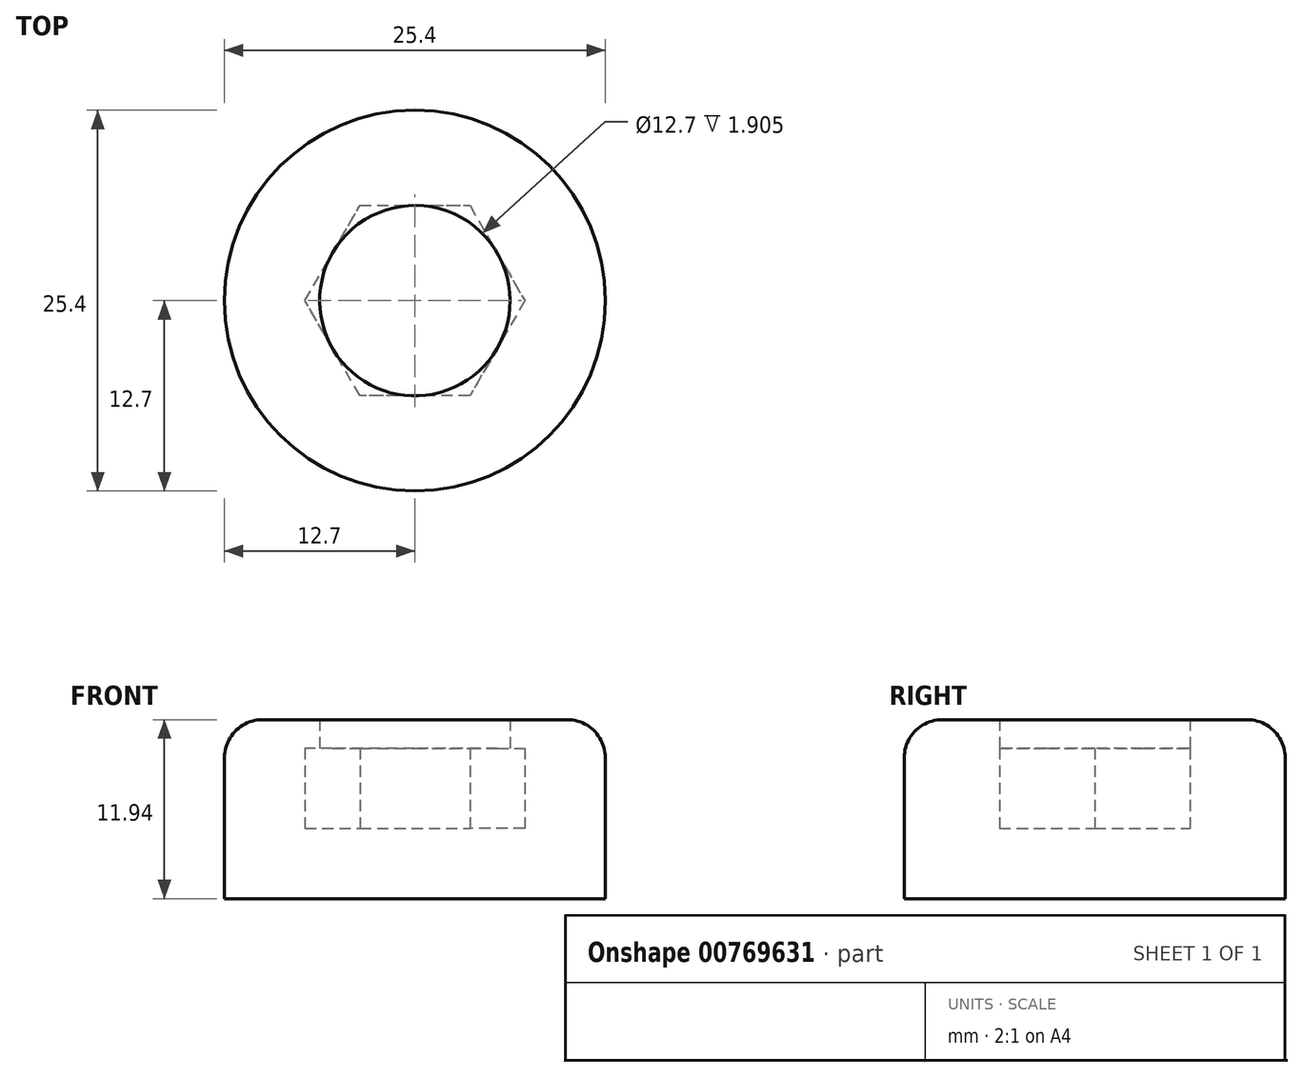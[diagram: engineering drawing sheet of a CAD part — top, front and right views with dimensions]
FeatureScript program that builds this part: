
annotation { "Feature Type Name" : "Feature", "Feature Type Description" : "" }
export const myFeature = defineFeature(function(context is Context, id is Id, definition is map)
    precondition{}
    {
        {
            var Q0;
            Q0=qCreatedBy(makeId("Top.planeOp"),FACE);
            var sketch = newSketch(context, id + "F0", { "sketchPlane" : qUnion([Q0])});
            skCircle(sketch, "E0.cCircle", {"center": v(0, 0) * mm, "radius": 6.35 * mm, "construction": true});
            skLineSegment(sketch, "E0.0", {"start": v(3.67, 6.35) * mm, "end": v(7.33, 0) * mm});
            skLineSegment(sketch, "E0.1", {"start": v(7.33, 0) * mm, "end": v(3.67, -6.35) * mm});
            skLineSegment(sketch, "E0.2", {"start": v(3.67, -6.35) * mm, "end": v(-3.67, -6.35) * mm});
            skLineSegment(sketch, "E0.3", {"start": v(-3.67, -6.35) * mm, "end": v(-7.33, 0) * mm});
            skLineSegment(sketch, "E0.4", {"start": v(-7.33, 0) * mm, "end": v(-3.67, 6.35) * mm});
            skLineSegment(sketch, "E0.5", {"start": v(-3.67, 6.35) * mm, "end": v(3.67, 6.35) * mm});
            skPoint(sketch, "E0.0.midPoint", {"position": v(5.5, 3.18) * mm});
            skCircle(sketch, "E1", {"center": v(0, 0) * mm, "radius": 12.7 * mm});
            skSolve(sketch);
        }
        {
            var Q0;
            Q0=makeQuery(id+"F0.imprint","IMPRINT",FACE,{"disambiguationData":[TD([[makeQuery(id+"F0.imprint","IMPRINT",EDGE,{"derivedFrom":sQuery(id+"F0.wireOp",EDGE,"E0.0")}),1.0]])]});
            var Q1;
            Q1=makeQuery(id+"F0.imprint","IMPRINT",FACE,{"disambiguationData":[TD([[makeQuery(id+"F0.imprint","IMPRINT",EDGE,{"derivedFrom":sQuery(id+"F0.wireOp",EDGE,"E0.0")}),-1.0]])]});
            extrude(context, id + "F1", {"entities" : qUnion([Q0, Q1]), "oppositeDirection" : true, "depth" : 4.7 * mm, "offsetDistance" : 25.4 * mm});
        }
        {
            var Q0;
            Q0=makeQuery(id+"F0.imprint","IMPRINT",FACE,{"disambiguationData":[TD([[makeQuery(id+"F0.imprint","IMPRINT",EDGE,{"derivedFrom":sQuery(id+"F0.wireOp",EDGE,"E0.0")}),1.0]])]});
            extrude(context, id + "F2", {"entities" : qUnion([Q0]), "operationType" : NewBodyOperationType.ADD, "depth" : 5.33 * mm, "offsetDistance" : 25.4 * mm});
        }
        {
            var Q0;
            Q0=makeQuery(id+"F2.opExtrude","CAP_FACE",FACE,{"disambiguationData":[OSD([sQuery(id+"F0.wireOp",EDGE,"E0.0"),sQuery(id+"F0.wireOp",EDGE,"E0.1"),sQuery(id+"F0.wireOp",EDGE,"E0.2"),sQuery(id+"F0.wireOp",EDGE,"E0.3"),sQuery(id+"F0.wireOp",EDGE,"E0.4"),sQuery(id+"F0.wireOp",EDGE,"E0.5"),sQuery(id+"F0.wireOp",EDGE,"E1")])],"isStart":false});
            var sketch = newSketch(context, id + "F3", { "sketchPlane" : qUnion([Q0])});
            skCircle(sketch, "E2", {"center": v(0, 0) * mm, "radius": 6.35 * mm});
            skSolve(sketch);
        }
        {
            var Q0;
            Q0=makeQuery(id+"F3.imprint","IMPRINT",FACE,{"disambiguationData":[TD([[makeQuery(id+"F3.imprint","IMPRINT",EDGE,{"derivedFrom":makeQuery(id+"F2.opExtrude","CAP_EDGE",EDGE,{"disambiguationData":[OSD([sQuery(id+"F0.wireOp",EDGE,"E1")])],"isStart":false})}),1.0]])]});
            var Q1;
            {var subQ0=sQuery(id+"F3.wireOp",EDGE,"E2");var subQ1=makeQuery(id+"F2.opExtrude","CAP_EDGE",EDGE,{"disambiguationData":[OSD([sQuery(id+"F0.wireOp",EDGE,"E0.5")])],"isStart":false});var subQ2=makeQuery(id+"F3.imprint","INTERSECT",VERTEX,{"derivedFrom":[subQ1,subQ0]});Q1=makeQuery(id+"F3.imprint","IMPRINT",FACE,{"disambiguationData":[TD([[makeQuery(id+"F3.imprint","IMPRINT",EDGE,{"disambiguationData":[TD([[subQ2,-1.0]])],"derivedFrom":subQ0}),-1.0]])]});}
            var Q2;
            {var subQ0=sQuery(id+"F3.wireOp",EDGE,"E2");var subQ1=makeQuery(id+"F2.opExtrude","CAP_EDGE",EDGE,{"disambiguationData":[OSD([sQuery(id+"F0.wireOp",EDGE,"E0.5")])],"isStart":false});var subQ2=makeQuery(id+"F3.imprint","INTERSECT",VERTEX,{"derivedFrom":[subQ1,subQ0]});Q2=makeQuery(id+"F3.imprint","IMPRINT",FACE,{"disambiguationData":[TD([[makeQuery(id+"F3.imprint","IMPRINT",EDGE,{"disambiguationData":[TD([[subQ2,1.0]])],"derivedFrom":subQ0}),-1.0]])]});}
            var Q3;
            {var subQ0=sQuery(id+"F3.wireOp",EDGE,"E2");var subQ1=makeQuery(id+"F2.opExtrude","CAP_EDGE",EDGE,{"disambiguationData":[OSD([sQuery(id+"F0.wireOp",EDGE,"E0.0")])],"isStart":false});var subQ2=makeQuery(id+"F3.imprint","INTERSECT",VERTEX,{"derivedFrom":[subQ1,subQ0]});Q3=makeQuery(id+"F3.imprint","IMPRINT",FACE,{"disambiguationData":[TD([[makeQuery(id+"F3.imprint","IMPRINT",EDGE,{"disambiguationData":[TD([[subQ2,1.0]])],"derivedFrom":subQ0}),-1.0]])]});}
            var Q4;
            {var subQ0=sQuery(id+"F3.wireOp",EDGE,"E2");var subQ1=makeQuery(id+"F2.opExtrude","CAP_EDGE",EDGE,{"disambiguationData":[OSD([sQuery(id+"F0.wireOp",EDGE,"E0.2")])],"isStart":false});var subQ2=makeQuery(id+"F3.imprint","INTERSECT",VERTEX,{"derivedFrom":[subQ1,subQ0]});Q4=makeQuery(id+"F3.imprint","IMPRINT",FACE,{"disambiguationData":[TD([[makeQuery(id+"F3.imprint","IMPRINT",EDGE,{"disambiguationData":[TD([[subQ2,-1.0]])],"derivedFrom":subQ0}),-1.0]])]});}
            var Q5;
            {var subQ0=sQuery(id+"F3.wireOp",EDGE,"E2");var subQ1=makeQuery(id+"F2.opExtrude","CAP_EDGE",EDGE,{"disambiguationData":[OSD([sQuery(id+"F0.wireOp",EDGE,"E0.3")])],"isStart":false});var subQ2=makeQuery(id+"F3.imprint","INTERSECT",VERTEX,{"derivedFrom":[subQ1,subQ0]});Q5=makeQuery(id+"F3.imprint","IMPRINT",FACE,{"disambiguationData":[TD([[makeQuery(id+"F3.imprint","IMPRINT",EDGE,{"disambiguationData":[TD([[subQ2,-1.0]])],"derivedFrom":subQ0}),-1.0]])]});}
            var Q6;
            {var subQ0=sQuery(id+"F3.wireOp",EDGE,"E2");var subQ1=makeQuery(id+"F2.opExtrude","CAP_EDGE",EDGE,{"disambiguationData":[OSD([sQuery(id+"F0.wireOp",EDGE,"E0.4")])],"isStart":false});var subQ2=makeQuery(id+"F3.imprint","INTERSECT",VERTEX,{"derivedFrom":[subQ1,subQ0]});Q6=makeQuery(id+"F3.imprint","IMPRINT",FACE,{"disambiguationData":[TD([[makeQuery(id+"F3.imprint","IMPRINT",EDGE,{"disambiguationData":[TD([[subQ2,-1.0]])],"derivedFrom":subQ0}),-1.0]])]});}
            extrude(context, id + "F4", {"entities" : qUnion([Q0, Q1, Q2, Q3, Q4, Q5, Q6]), "operationType" : NewBodyOperationType.ADD, "depth" : 1.9 * mm, "offsetDistance" : 25.4 * mm});
        }
        {
            var Q0;
            Q0=makeQuery(id+"F4.opExtrude","CAP_EDGE",EDGE,{"disambiguationData":[OSD([sQuery(id+"F0.wireOp",EDGE,"E1")])],"isStart":false});
            fillet(context, id + "F5", {"entities" : qUnion([Q0]), "radius" : 2.54 * mm, "tangentPropagation" : true, "allowEdgeOverflow" : false});
        }
    });
